# Revit family: Barrier_Gate_AutoGate_Prestigous
name_source: partatom
category: Generic Models
revit_build: Autodesk Revit 2015 (Build: 20140606_1530(x64)
units: mm (PartAtom-declared; Revit-internal decimal feet)

## types (2) — shared parameters
Assembly Code = E1030900
Construction Details = http://www.arcat.com
Default Elevation = 0' - 0"
Include Finials = No
Keynote = 32 21 00
Manufacturer = AutoGate, Inc
Manufacturer Fax = 419-588-3514
Manufacturer Website = http://autogate.com
Maximum Size = 25 x 8 ft (W x H)
Number of Interior Design Repeats = 36
Product Data = http://www.arcat.com
Revision = R1_2016-11
Sales Information = http://autogate.com
Specification = http://www.arcat.com
URL = http://autogate.com
zero-valued in all types: Expected Lifespan (Years), Maintenance Schedule (Months), Warranty Duration (Years)

## per-type parameters (varying)
| type | Description | Model |
| Size as Specified | AutoGate Prestigous Gate as Specified | Prestigous 800 |
| Size as Specified with Finials | AutoGate Prestigous Gate with Finials as Specified | Prestigous 800 with Finials |

## geometry (parser evidence)
native form markers: Sweep x5
no freeform markers — native parametric forms only
